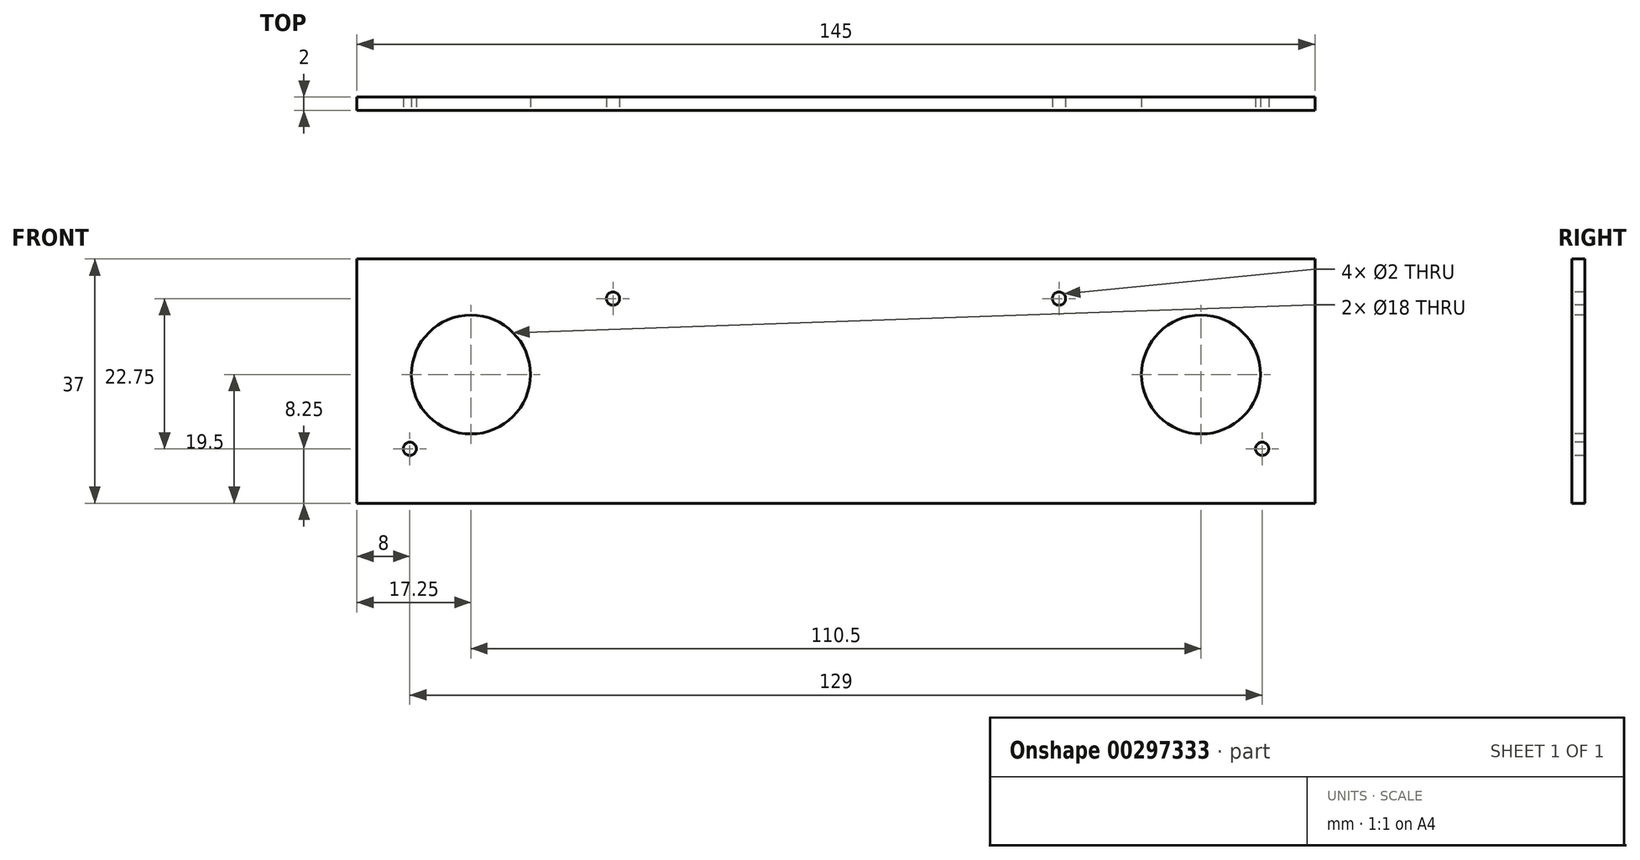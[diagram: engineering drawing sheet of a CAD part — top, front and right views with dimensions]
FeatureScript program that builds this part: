
annotation { "Feature Type Name" : "Feature", "Feature Type Description" : "" }
export const myFeature = defineFeature(function(context is Context, id is Id, definition is map)
    precondition{}
    {
        {
            var Q0;
            Q0=qCreatedBy(makeId("Front.planeOp"),FACE);
            var sketch = newSketch(context, id + "F0", { "sketchPlane" : qUnion([Q0])});
            skLineSegment(sketch, "E0.bottom", {"start": v(72.5, 17.5) * mm, "end": v(-72.5, 17.5) * mm});
            skLineSegment(sketch, "E0.top", {"start": v(72.5, -17.5) * mm, "end": v(-72.5, -17.5) * mm});
            skLineSegment(sketch, "E0.left", {"start": v(72.5, 17.5) * mm, "end": v(72.5, -17.5) * mm});
            skLineSegment(sketch, "E0.right", {"start": v(-72.5, 17.5) * mm, "end": v(-72.5, -17.5) * mm});
            skPoint(sketch, "E0.middle", {"position": v(0, 0) * mm});
            skSolve(sketch);
        }
        {
            var Q0;
            Q0 = qSketchRegion(id + "F0", true);
            extrude(context, id + "F1", {"entities" : qUnion([Q0]), "depth" : 2 * mm});
        }
        {
            var Q0;
            Q0=makeQuery(id+"F1.opExtrude","CAP_FACE",FACE,{"disambiguationData":[OSD([sQuery(id+"F0.wireOp",EDGE,"E0.bottom"),sQuery(id+"F0.wireOp",EDGE,"E0.top"),sQuery(id+"F0.wireOp",EDGE,"E0.left"),sQuery(id+"F0.wireOp",EDGE,"E0.right")])],"isStart":false});
            var sketch = newSketch(context, id + "F2", { "sketchPlane" : qUnion([Q0])});
            skLineSegment(sketch, "E1.bottom", {"start": v(33.75, 11.5) * mm, "end": v(-33.75, 11.5) * mm, "construction": true});
            skLineSegment(sketch, "E1.top", {"start": v(33.75, -11.5) * mm, "end": v(-33.75, -11.5) * mm, "construction": true});
            skLineSegment(sketch, "E1.left", {"start": v(33.75, 11.5) * mm, "end": v(33.75, -11.5) * mm, "construction": true});
            skLineSegment(sketch, "E1.right", {"start": v(-33.75, 11.5) * mm, "end": v(-33.75, -11.5) * mm, "construction": true});
            skPoint(sketch, "E1.middle", {"position": v(0, 0) * mm});
            skCircle(sketch, "E2", {"center": v(-33.75, 11.5) * mm, "radius": 1 * mm});
            skCircle(sketch, "E3", {"center": v(33.75, 11.5) * mm, "radius": 1 * mm});
            skSolve(sketch);
        }
        {
            var Q0;
            Q0 = qSketchRegion(id + "F2", true);
            extrude(context, id + "F3", {"entities" : qUnion([Q0]), "operationType" : NewBodyOperationType.REMOVE, "oppositeDirection" : true, "depth" : 25 * mm});
        }
        {
            var Q0;
            Q0=makeQuery(id+"F1.opExtrude","CAP_FACE",FACE,{"disambiguationData":[OSD([sQuery(id+"F0.wireOp",EDGE,"E0.bottom"),sQuery(id+"F0.wireOp",EDGE,"E0.top"),sQuery(id+"F0.wireOp",EDGE,"E0.left"),sQuery(id+"F0.wireOp",EDGE,"E0.right")])],"isStart":false});
            var sketch = newSketch(context, id + "F4", { "sketchPlane" : qUnion([Q0])});
            skCircle(sketch, "E4", {"center": v(-64.5, -11.25) * mm, "radius": 1 * mm});
            skCircle(sketch, "E5", {"center": v(64.5, -11.25) * mm, "radius": 1 * mm});
            skSolve(sketch);
        }
        {
            var Q0;
            Q0 = qSketchRegion(id + "F4", true);
            extrude(context, id + "F5", {"entities" : qUnion([Q0]), "operationType" : NewBodyOperationType.REMOVE, "oppositeDirection" : true, "depth" : 25 * mm});
        }
        {
            var Q0;
            Q0=makeQuery(id+"F1.opExtrude","CAP_FACE",FACE,{"disambiguationData":[OSD([sQuery(id+"F0.wireOp",EDGE,"E0.bottom"),sQuery(id+"F0.wireOp",EDGE,"E0.top"),sQuery(id+"F0.wireOp",EDGE,"E0.left"),sQuery(id+"F0.wireOp",EDGE,"E0.right")])],"isStart":false});
            var sketch = newSketch(context, id + "F6", { "sketchPlane" : qUnion([Q0])});
            skCircle(sketch, "E6", {"center": v(-55.25, 0) * mm, "radius": 9 * mm});
            skCircle(sketch, "E7", {"center": v(55.25, 0) * mm, "radius": 9 * mm});
            skSolve(sketch);
        }
        {
            var Q0;
            Q0 = qSketchRegion(id + "F6", true);
            extrude(context, id + "F7", {"entities" : qUnion([Q0]), "operationType" : NewBodyOperationType.REMOVE, "oppositeDirection" : true, "depth" : 25 * mm});
        }
        {
            var Q0;
            Q0=makeQuery(id+"F1.opExtrude","SWEPT_FACE",FACE,{"disambiguationData":[OSD([sQuery(id+"F0.wireOp",EDGE,"E0.top")])]});
            var sketch = newSketch(context, id + "F8", { "sketchPlane" : qUnion([Q0])});
            skLineSegment(sketch, "E8.bottom", {"start": v(-72.5, 2) * mm, "end": v(72.5, 2) * mm});
            skLineSegment(sketch, "E8.top", {"start": v(-72.5, 0) * mm, "end": v(72.5, 0) * mm});
            skLineSegment(sketch, "E8.left", {"start": v(-72.5, 2) * mm, "end": v(-72.5, 0) * mm});
            skLineSegment(sketch, "E8.right", {"start": v(72.5, 2) * mm, "end": v(72.5, 0) * mm});
            skSolve(sketch);
        }
        {
            var Q0;
            Q0 = qSketchRegion(id + "F8", true);
            extrude(context, id + "F9", {"entities" : qUnion([Q0]), "operationType" : NewBodyOperationType.ADD, "depth" : 2 * mm});
        }
    });
